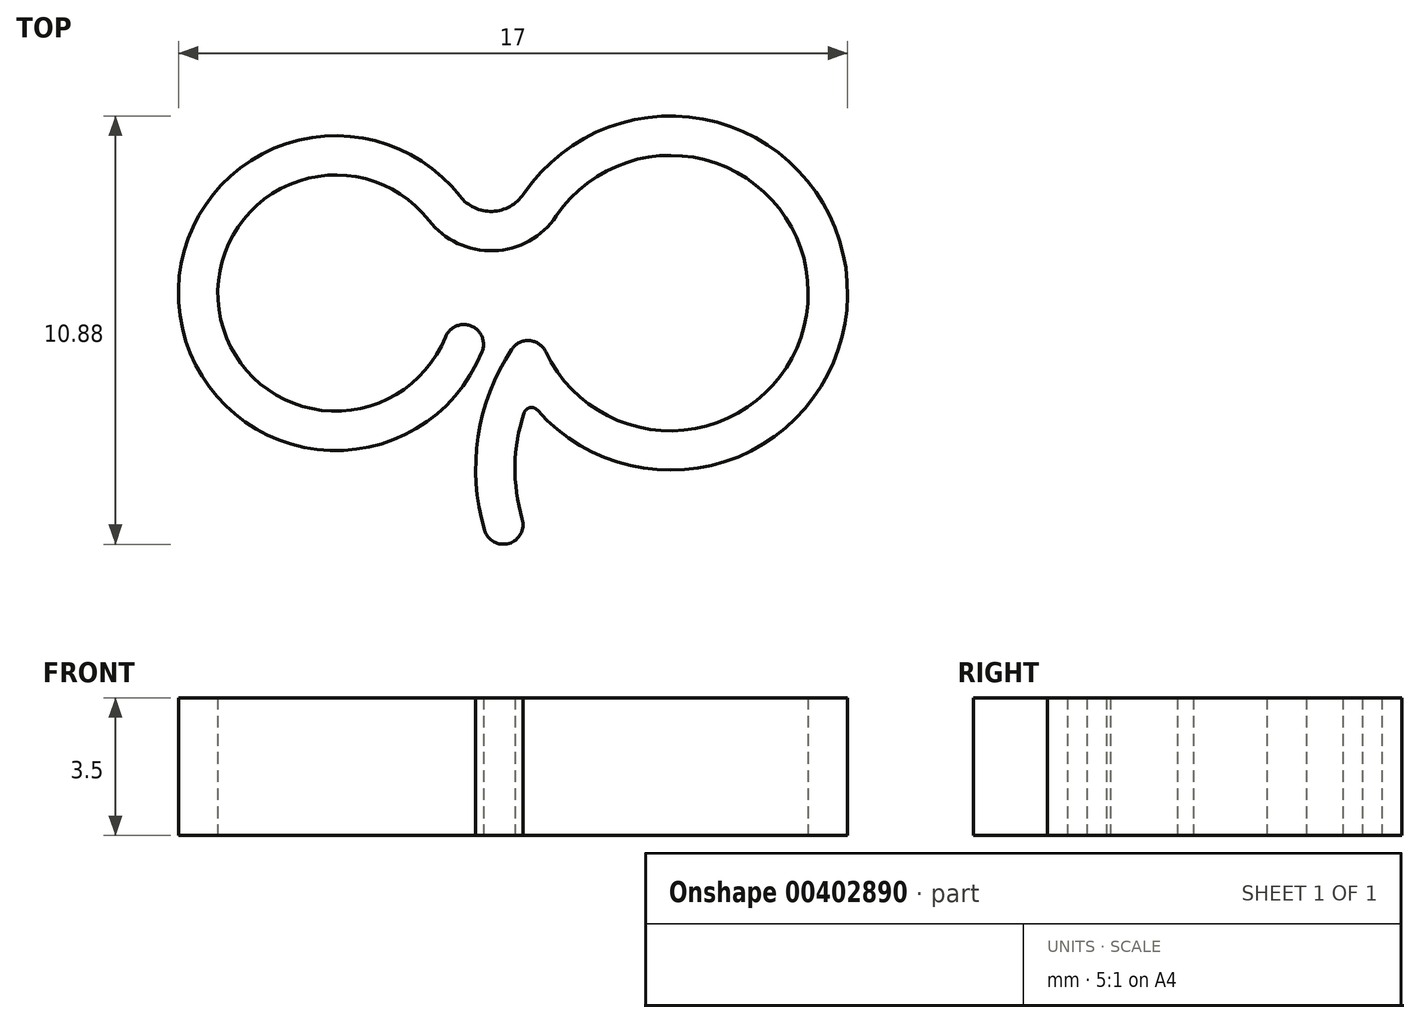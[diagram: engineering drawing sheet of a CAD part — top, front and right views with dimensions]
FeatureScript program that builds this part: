
annotation { "Feature Type Name" : "Feature", "Feature Type Description" : "" }
export const myFeature = defineFeature(function(context is Context, id is Id, definition is map)
    precondition{}
    {
        {
            var Q0;
            Q0=qCreatedBy(makeId("Top.planeOp"),FACE);
            var sketch = newSketch(context, id + "F0", { "sketchPlane" : qUnion([Q0])});
            skLineSegment(sketch, "E0", {"start": v(0, 0) * mm, "end": v(-8.5, 0) * mm, "construction": true});
            skArc(sketch, "E1", {"start": v(-5.35, 2.46) * mm, "mid": v(-9.81, 3.78) * mm, "end": v(-12.5, -0.02) * mm});
            skArc(sketch, "E2", {"start": v(-12.5, -0.02) * mm, "mid": v(-9.24, -3.93) * mm, "end": v(-4.79, -1.48) * mm});
            skArc(sketch, "E3", {"start": v(-4.5, 0) * mm, "mid": v(-4.27, -1.43) * mm, "end": v(-3.6, -2.71) * mm, "construction": true});
            skArc(sketch, "E4", {"start": v(4.5, 0) * mm, "mid": v(1.32, 4.3) * mm, "end": v(-3.73, 2.52) * mm});
            skPoint(sketch, "E5.visualSharp", {"position": v(-4.5, 0) * mm});
            skArc(sketch, "E5.filletArc", {"start": v(-5.35, 2.46) * mm, "mid": v(-4.52, 2.08) * mm, "end": v(-3.73, 2.52) * mm});
            skArc(sketch, "E6", {"start": v(-6.14, 1.85) * mm, "mid": v(-9.5, 2.83) * mm, "end": v(-11.5, -0.06) * mm});
            skArc(sketch, "E7", {"start": v(-11.5, -0.06) * mm, "mid": v(-9.04, -2.95) * mm, "end": v(-5.71, -1.11) * mm});
            skArc(sketch, "E8", {"start": v(-3.5, 0) * mm, "mid": v(-3.48, -0.34) * mm, "end": v(-3.43, -0.68) * mm, "construction": true});
            skArc(sketch, "E9", {"start": v(3.5, 0.05) * mm, "mid": v(1, 3.35) * mm, "end": v(-2.9, 1.96) * mm});
            skArc(sketch, "E10.filletArc", {"start": v(-6.14, 1.85) * mm, "mid": v(-4.49, 1.08) * mm, "end": v(-2.9, 1.96) * mm});
            skLineSegment(sketch, "E11", {"start": v(-4.98, -0.88) * mm, "end": v(-4.98, -0.88) * mm});
            skArc(sketch, "E12.filletArc", {"start": v(-4.98, -0.88) * mm, "mid": v(-5.4, -0.82) * mm, "end": v(-5.71, -1.11) * mm});
            skArc(sketch, "E13.filletArc", {"start": v(-4.79, -1.48) * mm, "mid": v(-4.77, -1.14) * mm, "end": v(-4.98, -0.88) * mm});
            skArc(sketch, "E14", {"start": v(-3.17, -1.5) * mm, "mid": v(0.79, -3.41) * mm, "end": v(3.5, 0.05) * mm});
            skArc(sketch, "E15", {"start": v(-3.38, -2.97) * mm, "mid": v(1.59, -4.21) * mm, "end": v(4.5, 0) * mm});
            skLineSegment(sketch, "E16", {"start": v(-4.06, -6.34) * mm, "end": v(-4.06, -6.34) * mm});
            skArc(sketch, "E17", {"start": v(-3.72, -3.04) * mm, "mid": v(-3.95, -4.39) * mm, "end": v(-3.77, -5.74) * mm});
            skArc(sketch, "E18", {"start": v(-4.03, -1.43) * mm, "mid": v(-4.89, -3.65) * mm, "end": v(-4.72, -6.02) * mm});
            skPoint(sketch, "E19.visualSharp", {"position": v(-3.43, -0.68) * mm});
            skArc(sketch, "E19.filletArc", {"start": v(-3.17, -1.5) * mm, "mid": v(-3.58, -1.2) * mm, "end": v(-4.03, -1.43) * mm});
            skPoint(sketch, "E20.visualSharp", {"position": v(-3.62, -6.16) * mm});
            skArc(sketch, "E20.filletArc", {"start": v(-4.06, -6.34) * mm, "mid": v(-3.8, -6.1) * mm, "end": v(-3.77, -5.74) * mm});
            skPoint(sketch, "E21.visualSharp", {"position": v(-4.54, -6.54) * mm});
            skArc(sketch, "E21.filletArc", {"start": v(-4.72, -6.02) * mm, "mid": v(-4.46, -6.33) * mm, "end": v(-4.06, -6.34) * mm});
            skPoint(sketch, "E22.visualSharp", {"position": v(-3.6, -2.71) * mm});
            skArc(sketch, "E22.filletArc", {"start": v(-3.38, -2.97) * mm, "mid": v(-3.57, -2.9) * mm, "end": v(-3.72, -3.04) * mm});
            skSolve(sketch);
        }
        {
            var Q0;
            Q0=makeQuery(id+"F0.imprint","IMPRINT",FACE,{"disambiguationData":[TD([[makeQuery(id+"F0.imprint","IMPRINT",EDGE,{"derivedFrom":sQuery(id+"F0.wireOp",EDGE,"E1")}),1.0]])]});
            extrude(context, id + "F1", {"entities" : qUnion([Q0]), "depth" : 3.5 * mm});
        }
    });
